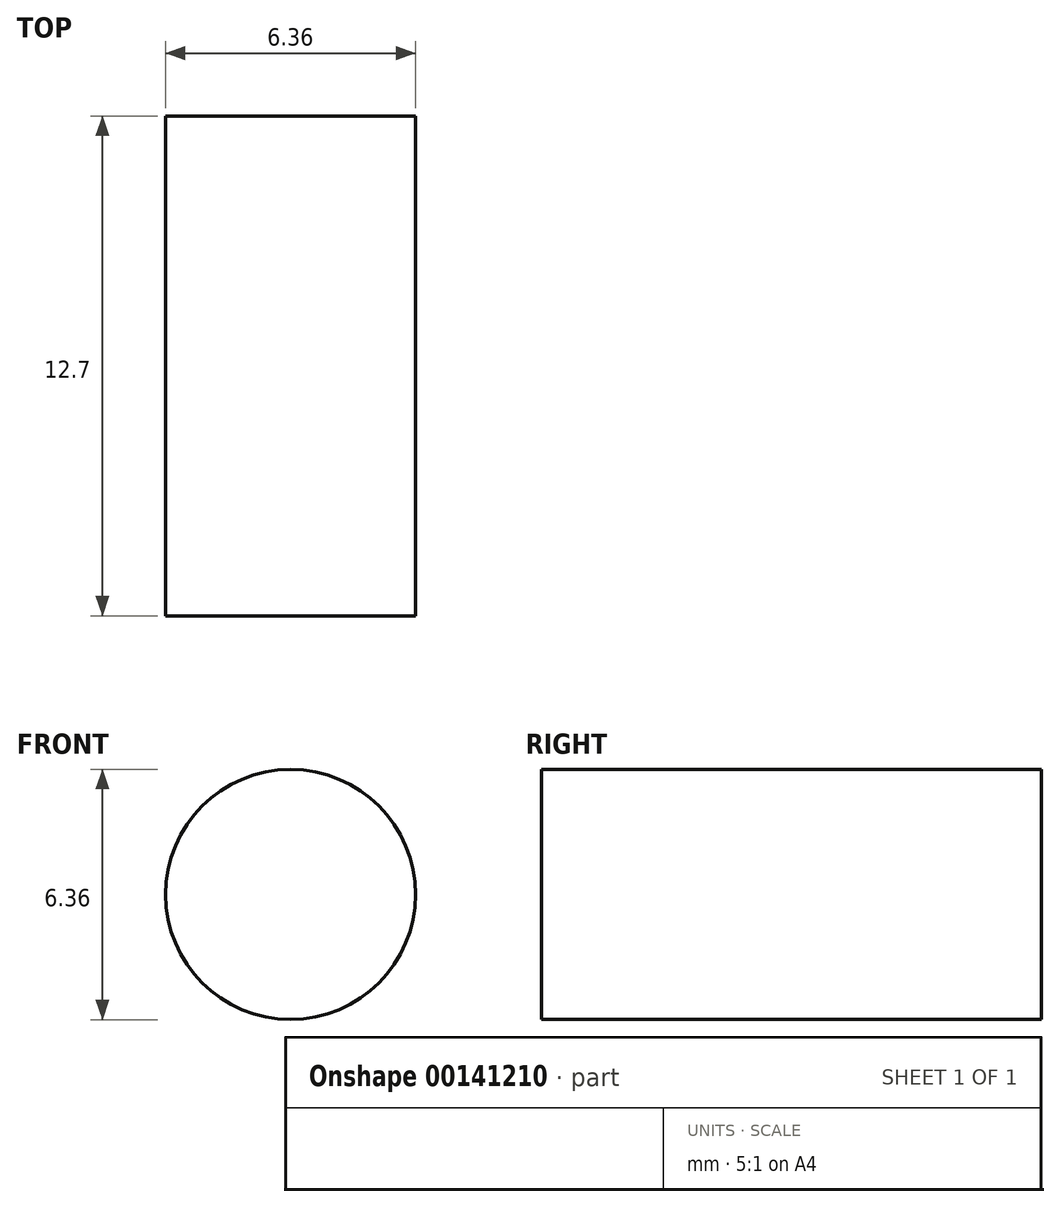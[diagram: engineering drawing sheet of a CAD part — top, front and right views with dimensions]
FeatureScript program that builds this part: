
annotation { "Feature Type Name" : "Feature", "Feature Type Description" : "" }
export const myFeature = defineFeature(function(context is Context, id is Id, definition is map)
    precondition{}
    {
        {
            var Q0;
            Q0=qCreatedBy(makeId("Front.planeOp"),FACE);
            var sketch = newSketch(context, id + "F0", { "sketchPlane" : qUnion([Q0])});
            skCircle(sketch, "E0", {"center": v(0, 0) * mm, "radius": 3.18 * mm});
            skSolve(sketch);
        }
        {
            var Q0;
            Q0=makeQuery(id+"F0.imprint","IMPRINT",FACE,{"disambiguationData":[TD([[makeQuery(id+"F0.imprint","IMPRINT",EDGE,{"derivedFrom":sQuery(id+"F0.wireOp",EDGE,"E0")}),1.0]])]});
            extrude(context, id + "F1", {"entities" : qUnion([Q0]), "depth" : 12.7 * mm});
        }
    });
